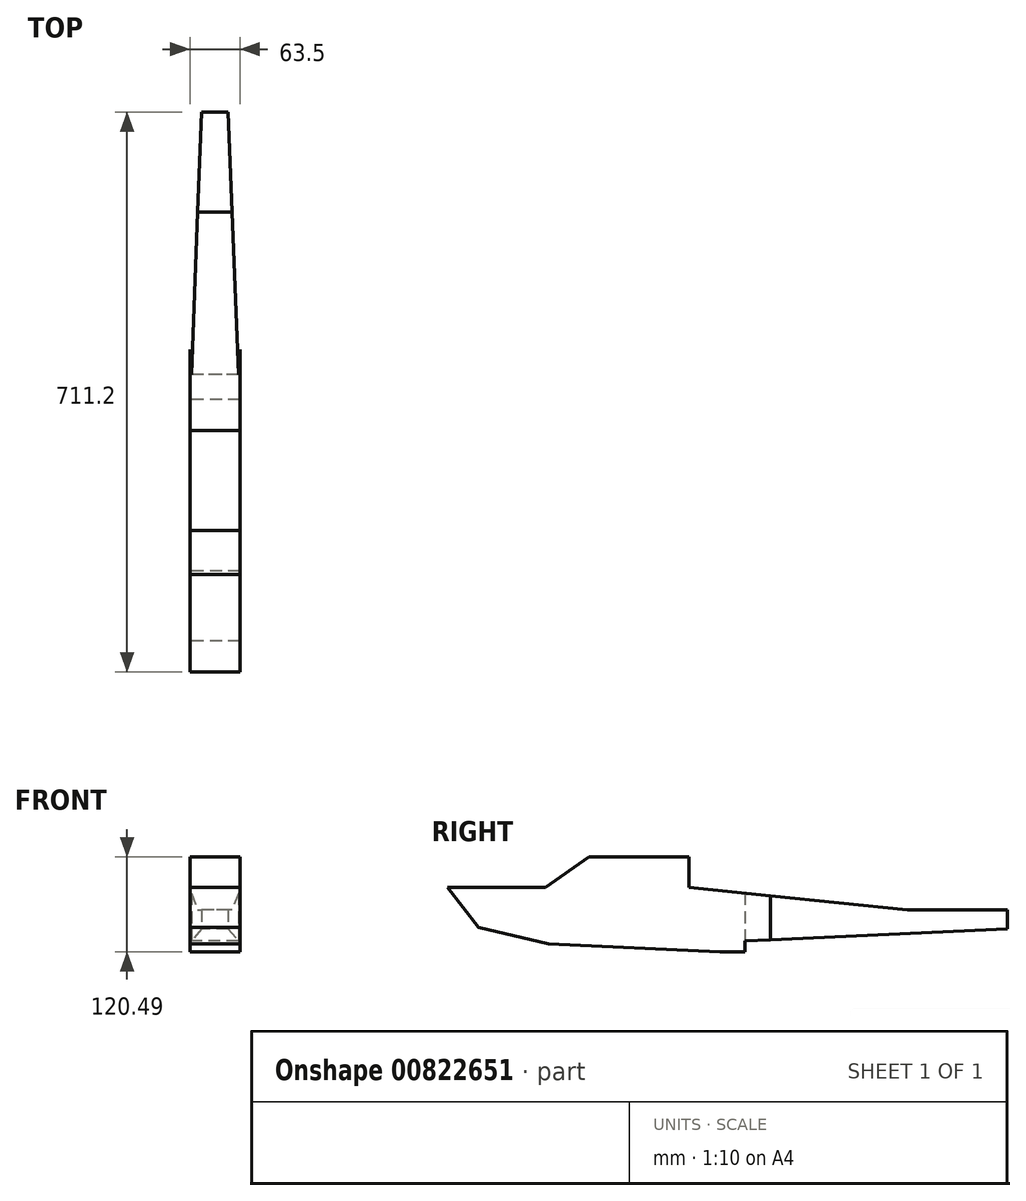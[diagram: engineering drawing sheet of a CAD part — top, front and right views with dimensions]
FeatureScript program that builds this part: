
annotation { "Feature Type Name" : "Feature", "Feature Type Description" : "" }
export const myFeature = defineFeature(function(context is Context, id is Id, definition is map)
    precondition{}
    {
        {
            var Q0;
            Q0=qCreatedBy(makeId("Right.planeOp"),FACE);
            var sketch = newSketch(context, id + "F0", { "sketchPlane" : qUnion([Q0])});
            skLineSegment(sketch, "E0", {"start": v(333.27, 29.15) * mm, "end": v(333.27, 53.14) * mm});
            skLineSegment(sketch, "E1", {"start": v(-71.46, 81.74) * mm, "end": v(-71.46, 120.49) * mm});
            skLineSegment(sketch, "E2", {"start": v(-71.46, 120.49) * mm, "end": v(-198.46, 120.49) * mm});
            skLineSegment(sketch, "E3", {"start": v(-198.46, 120.49) * mm, "end": v(-253.81, 81.74) * mm});
            skLineSegment(sketch, "E4", {"start": v(-253.81, 81.74) * mm, "end": v(-377.93, 81.74) * mm});
            skLineSegment(sketch, "E5", {"start": v(333.27, 53.14) * mm, "end": v(206.27, 53.14) * mm});
            skLineSegment(sketch, "E6", {"start": v(206.27, 53.14) * mm, "end": v(-71.46, 81.74) * mm});
            skLineSegment(sketch, "E7", {"start": v(-32.05, 0) * mm, "end": v(-249.62, 9.9) * mm});
            skLineSegment(sketch, "E8", {"start": v(-338.52, 31.11) * mm, "end": v(-249.62, 9.9) * mm});
            skLineSegment(sketch, "E9", {"start": v(-338.52, 31.11) * mm, "end": v(-377.93, 81.74) * mm});
            skLineSegment(sketch, "E10", {"start": v(-32.05, 0) * mm, "end": v(0, 0) * mm});
            skLineSegment(sketch, "E11", {"start": v(0, 0) * mm, "end": v(0, 13.81) * mm});
            skLineSegment(sketch, "E12", {"start": v(0, 13.81) * mm, "end": v(333.27, 29.15) * mm});
            skSolve(sketch);
        }
        {
            var Q0;
            Q0 = qSketchRegion(id + "F0", true);
            extrude(context, id + "F1", {"entities" : qUnion([Q0]), "endBound" : BoundingType.SYMMETRIC, "depth" : 63.5 * mm, "offsetDistance" : 25.4 * mm});
        }
        {
            var Q0;
            Q0=qCreatedBy(makeId("Top.planeOp"),FACE);
            var sketch = newSketch(context, id + "F2", { "sketchPlane" : qUnion([Q0])});
            skLineSegment(sketch, "E13", {"start": v(-29.78, 0) * mm, "end": v(-12.7, 441.58) * mm});
            skLineSegment(sketch, "E14", {"start": v(-12.7, 441.58) * mm, "end": v(-57.1, 441.58) * mm});
            skLineSegment(sketch, "E15.MirrorCS", {"start": v(29.78, 0) * mm, "end": v(12.7, 441.58) * mm});
            skLineSegment(sketch, "E16.MirrorCS", {"start": v(12.7, 441.58) * mm, "end": v(57.1, 441.58) * mm});
            skLineSegment(sketch, "E17", {"start": v(57.1, 441.58) * mm, "end": v(29.78, 0) * mm});
            skLineSegment(sketch, "E18", {"start": v(-57.1, 441.58) * mm, "end": v(-29.78, 0) * mm});
            skSolve(sketch);
        }
        {
            var Q0;
            Q0 = qSketchRegion(id + "F2", true);
            extrude(context, id + "F3", {"entities" : qUnion([Q0]), "operationType" : NewBodyOperationType.REMOVE, "depth" : 101.6 * mm, "offsetDistance" : 25.4 * mm});
        }
    });
